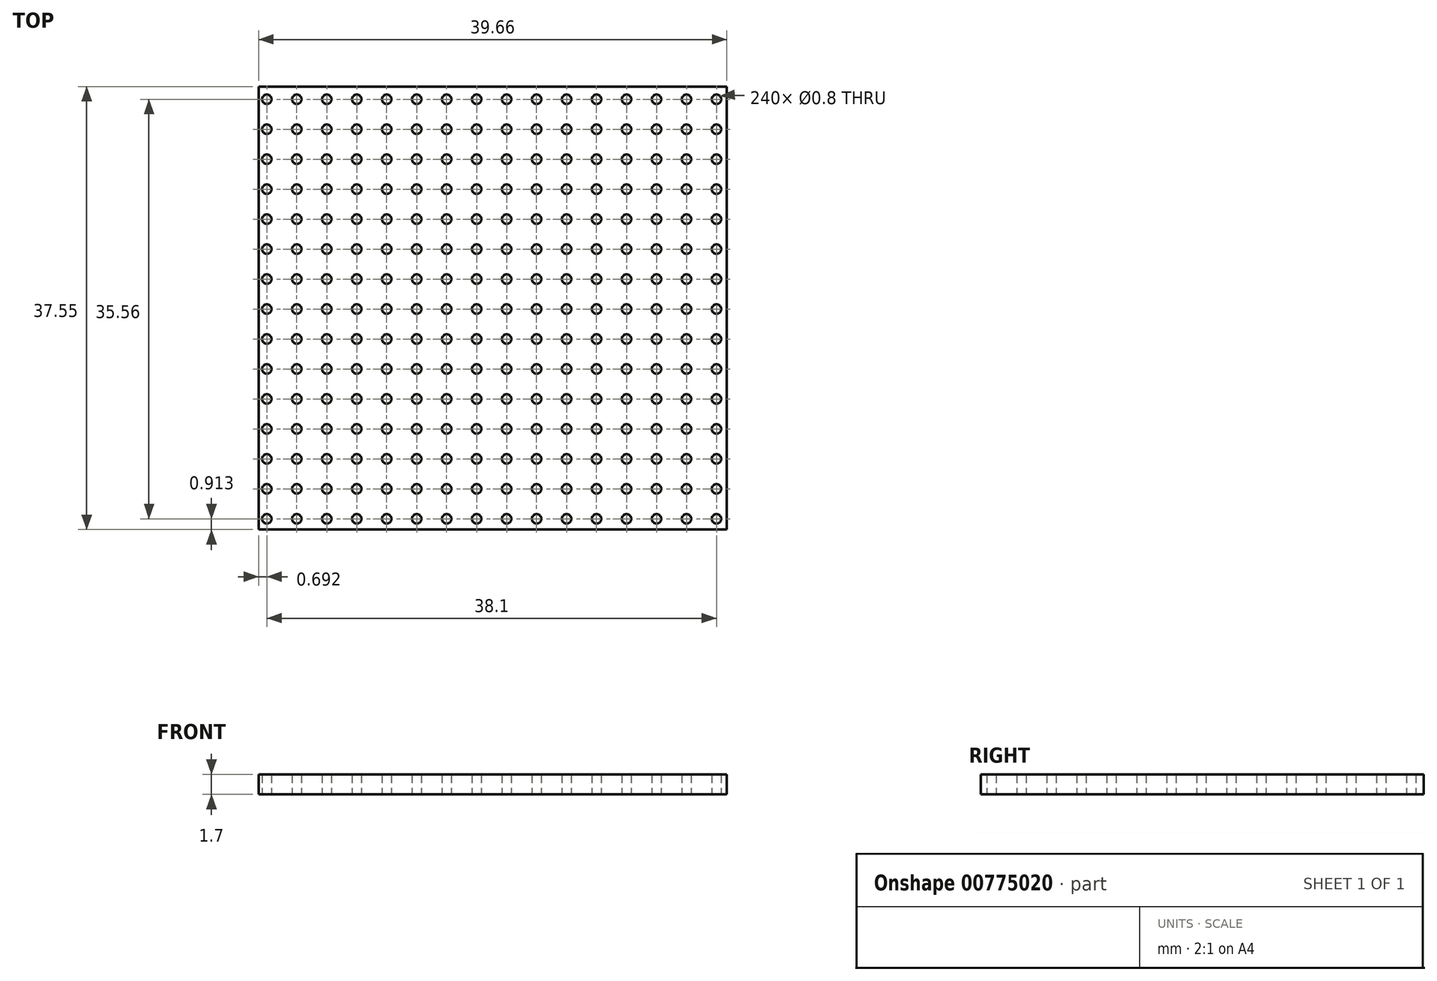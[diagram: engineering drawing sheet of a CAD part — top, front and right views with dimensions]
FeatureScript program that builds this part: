
annotation { "Feature Type Name" : "Feature", "Feature Type Description" : "" }
export const myFeature = defineFeature(function(context is Context, id is Id, definition is map)
    precondition{}
    {
        {
            var Q0;
            Q0=qCreatedBy(makeId("Top.planeOp"),FACE);
            var sketch = newSketch(context, id + "F0", { "sketchPlane" : qUnion([Q0])});
            skCircle(sketch, "E0", {"center": v(-31, -33.54) * mm, "radius": 0.4 * mm});
            skCircle(sketch, "E1.1.0.0", {"center": v(-28.47, -33.54) * mm, "radius": 0.4 * mm});
            skCircle(sketch, "E1.2.0.0", {"center": v(-25.93, -33.54) * mm, "radius": 0.4 * mm});
            skCircle(sketch, "E1.3.0.0", {"center": v(-23.39, -33.54) * mm, "radius": 0.4 * mm});
            skCircle(sketch, "E1.4.0.0", {"center": v(-20.85, -33.54) * mm, "radius": 0.4 * mm});
            skCircle(sketch, "E1.5.0.0", {"center": v(-18.3, -33.54) * mm, "radius": 0.4 * mm});
            skCircle(sketch, "E1.6.0.0", {"center": v(-15.77, -33.54) * mm, "radius": 0.4 * mm});
            skCircle(sketch, "E1.7.0.0", {"center": v(-13.23, -33.54) * mm, "radius": 0.4 * mm});
            skCircle(sketch, "E1.8.0.0", {"center": v(-10.69, -33.54) * mm, "radius": 0.4 * mm});
            skCircle(sketch, "E1.9.0.0", {"center": v(-8.15, -33.54) * mm, "radius": 0.4 * mm});
            skCircle(sketch, "E1.10.0.0", {"center": v(-5.6, -33.54) * mm, "radius": 0.4 * mm});
            skCircle(sketch, "E1.11.0.0", {"center": v(-3.07, -33.54) * mm, "radius": 0.4 * mm});
            skCircle(sketch, "E1.12.0.0", {"center": v(-0.53, -33.54) * mm, "radius": 0.4 * mm});
            skCircle(sketch, "E1.13.0.0", {"center": v(2.01, -33.54) * mm, "radius": 0.4 * mm});
            skCircle(sketch, "E1.14.0.0", {"center": v(4.55, -33.54) * mm, "radius": 0.4 * mm});
            skCircle(sketch, "E1.15.0.0", {"center": v(7.1, -33.54) * mm, "radius": 0.4 * mm});
            skLineSegment(sketch, "E1.direction1", {"start": v(-31, -33.54) * mm, "end": v(-28.47, -33.54) * mm, "construction": true});
            skCircle(sketch, "E2.1.0.0", {"center": v(2.01, -31) * mm, "radius": 0.4 * mm});
            skCircle(sketch, "E2.1.0.1", {"center": v(-0.53, -31) * mm, "radius": 0.4 * mm});
            skCircle(sketch, "E2.1.0.2", {"center": v(-3.07, -31) * mm, "radius": 0.4 * mm});
            skCircle(sketch, "E2.1.0.3", {"center": v(-5.6, -31) * mm, "radius": 0.4 * mm});
            skCircle(sketch, "E2.1.0.4", {"center": v(7.1, -31) * mm, "radius": 0.4 * mm});
            skCircle(sketch, "E2.1.0.5", {"center": v(-8.15, -31) * mm, "radius": 0.4 * mm});
            skCircle(sketch, "E2.1.0.6", {"center": v(-10.69, -31) * mm, "radius": 0.4 * mm});
            skCircle(sketch, "E2.1.0.7", {"center": v(4.55, -31) * mm, "radius": 0.4 * mm});
            skCircle(sketch, "E2.1.0.8", {"center": v(-13.23, -31) * mm, "radius": 0.4 * mm});
            skCircle(sketch, "E2.1.0.9", {"center": v(-15.77, -31) * mm, "radius": 0.4 * mm});
            skCircle(sketch, "E2.1.0.10", {"center": v(-18.3, -31) * mm, "radius": 0.4 * mm});
            skCircle(sketch, "E2.1.0.11", {"center": v(-20.85, -31) * mm, "radius": 0.4 * mm});
            skCircle(sketch, "E2.1.0.12", {"center": v(-23.39, -31) * mm, "radius": 0.4 * mm});
            skCircle(sketch, "E2.1.0.13", {"center": v(-25.93, -31) * mm, "radius": 0.4 * mm});
            skCircle(sketch, "E2.1.0.14", {"center": v(-28.47, -31) * mm, "radius": 0.4 * mm});
            skCircle(sketch, "E2.1.0.15", {"center": v(-31, -31) * mm, "radius": 0.4 * mm});
            skLineSegment(sketch, "E2.1.0.16", {"start": v(-31, -31) * mm, "end": v(-28.47, -31) * mm, "construction": true});
            skCircle(sketch, "E2.2.0.0", {"center": v(2.01, -28.46) * mm, "radius": 0.4 * mm});
            skCircle(sketch, "E2.2.0.1", {"center": v(-0.53, -28.46) * mm, "radius": 0.4 * mm});
            skCircle(sketch, "E2.2.0.2", {"center": v(-3.07, -28.46) * mm, "radius": 0.4 * mm});
            skCircle(sketch, "E2.2.0.3", {"center": v(-5.6, -28.46) * mm, "radius": 0.4 * mm});
            skCircle(sketch, "E2.2.0.4", {"center": v(7.1, -28.46) * mm, "radius": 0.4 * mm});
            skCircle(sketch, "E2.2.0.5", {"center": v(-8.15, -28.46) * mm, "radius": 0.4 * mm});
            skCircle(sketch, "E2.2.0.6", {"center": v(-10.69, -28.46) * mm, "radius": 0.4 * mm});
            skCircle(sketch, "E2.2.0.7", {"center": v(4.55, -28.46) * mm, "radius": 0.4 * mm});
            skCircle(sketch, "E2.2.0.8", {"center": v(-13.23, -28.46) * mm, "radius": 0.4 * mm});
            skCircle(sketch, "E2.2.0.9", {"center": v(-15.77, -28.46) * mm, "radius": 0.4 * mm});
            skCircle(sketch, "E2.2.0.10", {"center": v(-18.3, -28.46) * mm, "radius": 0.4 * mm});
            skCircle(sketch, "E2.2.0.11", {"center": v(-20.85, -28.46) * mm, "radius": 0.4 * mm});
            skCircle(sketch, "E2.2.0.12", {"center": v(-23.39, -28.46) * mm, "radius": 0.4 * mm});
            skCircle(sketch, "E2.2.0.13", {"center": v(-25.93, -28.46) * mm, "radius": 0.4 * mm});
            skCircle(sketch, "E2.2.0.14", {"center": v(-28.47, -28.46) * mm, "radius": 0.4 * mm});
            skCircle(sketch, "E2.2.0.15", {"center": v(-31, -28.46) * mm, "radius": 0.4 * mm});
            skLineSegment(sketch, "E2.2.0.16", {"start": v(-31, -28.46) * mm, "end": v(-28.47, -28.46) * mm, "construction": true});
            skCircle(sketch, "E2.3.0.0", {"center": v(2.01, -25.92) * mm, "radius": 0.4 * mm});
            skCircle(sketch, "E2.3.0.1", {"center": v(-0.53, -25.92) * mm, "radius": 0.4 * mm});
            skCircle(sketch, "E2.3.0.2", {"center": v(-3.07, -25.92) * mm, "radius": 0.4 * mm});
            skCircle(sketch, "E2.3.0.3", {"center": v(-5.6, -25.92) * mm, "radius": 0.4 * mm});
            skCircle(sketch, "E2.3.0.4", {"center": v(7.1, -25.92) * mm, "radius": 0.4 * mm});
            skCircle(sketch, "E2.3.0.5", {"center": v(-8.15, -25.92) * mm, "radius": 0.4 * mm});
            skCircle(sketch, "E2.3.0.6", {"center": v(-10.69, -25.92) * mm, "radius": 0.4 * mm});
            skCircle(sketch, "E2.3.0.7", {"center": v(4.55, -25.92) * mm, "radius": 0.4 * mm});
            skCircle(sketch, "E2.3.0.8", {"center": v(-13.23, -25.92) * mm, "radius": 0.4 * mm});
            skCircle(sketch, "E2.3.0.9", {"center": v(-15.77, -25.92) * mm, "radius": 0.4 * mm});
            skCircle(sketch, "E2.3.0.10", {"center": v(-18.3, -25.92) * mm, "radius": 0.4 * mm});
            skCircle(sketch, "E2.3.0.11", {"center": v(-20.85, -25.92) * mm, "radius": 0.4 * mm});
            skCircle(sketch, "E2.3.0.12", {"center": v(-23.39, -25.92) * mm, "radius": 0.4 * mm});
            skCircle(sketch, "E2.3.0.13", {"center": v(-25.93, -25.92) * mm, "radius": 0.4 * mm});
            skCircle(sketch, "E2.3.0.14", {"center": v(-28.47, -25.92) * mm, "radius": 0.4 * mm});
            skCircle(sketch, "E2.3.0.15", {"center": v(-31, -25.92) * mm, "radius": 0.4 * mm});
            skLineSegment(sketch, "E2.3.0.16", {"start": v(-31, -25.92) * mm, "end": v(-28.47, -25.92) * mm, "construction": true});
            skCircle(sketch, "E2.4.0.0", {"center": v(2.01, -23.38) * mm, "radius": 0.4 * mm});
            skCircle(sketch, "E2.4.0.1", {"center": v(-0.53, -23.38) * mm, "radius": 0.4 * mm});
            skCircle(sketch, "E2.4.0.2", {"center": v(-3.07, -23.38) * mm, "radius": 0.4 * mm});
            skCircle(sketch, "E2.4.0.3", {"center": v(-5.6, -23.38) * mm, "radius": 0.4 * mm});
            skCircle(sketch, "E2.4.0.4", {"center": v(7.1, -23.38) * mm, "radius": 0.4 * mm});
            skCircle(sketch, "E2.4.0.5", {"center": v(-8.15, -23.38) * mm, "radius": 0.4 * mm});
            skCircle(sketch, "E2.4.0.6", {"center": v(-10.69, -23.38) * mm, "radius": 0.4 * mm});
            skCircle(sketch, "E2.4.0.7", {"center": v(4.55, -23.38) * mm, "radius": 0.4 * mm});
            skCircle(sketch, "E2.4.0.8", {"center": v(-13.23, -23.38) * mm, "radius": 0.4 * mm});
            skCircle(sketch, "E2.4.0.9", {"center": v(-15.77, -23.38) * mm, "radius": 0.4 * mm});
            skCircle(sketch, "E2.4.0.10", {"center": v(-18.3, -23.38) * mm, "radius": 0.4 * mm});
            skCircle(sketch, "E2.4.0.11", {"center": v(-20.85, -23.38) * mm, "radius": 0.4 * mm});
            skCircle(sketch, "E2.4.0.12", {"center": v(-23.39, -23.38) * mm, "radius": 0.4 * mm});
            skCircle(sketch, "E2.4.0.13", {"center": v(-25.93, -23.38) * mm, "radius": 0.4 * mm});
            skCircle(sketch, "E2.4.0.14", {"center": v(-28.47, -23.38) * mm, "radius": 0.4 * mm});
            skCircle(sketch, "E2.4.0.15", {"center": v(-31, -23.38) * mm, "radius": 0.4 * mm});
            skLineSegment(sketch, "E2.4.0.16", {"start": v(-31, -23.38) * mm, "end": v(-28.47, -23.38) * mm, "construction": true});
            skCircle(sketch, "E2.5.0.0", {"center": v(2.01, -20.84) * mm, "radius": 0.4 * mm});
            skCircle(sketch, "E2.5.0.1", {"center": v(-0.53, -20.84) * mm, "radius": 0.4 * mm});
            skCircle(sketch, "E2.5.0.2", {"center": v(-3.07, -20.84) * mm, "radius": 0.4 * mm});
            skCircle(sketch, "E2.5.0.3", {"center": v(-5.6, -20.84) * mm, "radius": 0.4 * mm});
            skCircle(sketch, "E2.5.0.4", {"center": v(7.1, -20.84) * mm, "radius": 0.4 * mm});
            skCircle(sketch, "E2.5.0.5", {"center": v(-8.15, -20.84) * mm, "radius": 0.4 * mm});
            skCircle(sketch, "E2.5.0.6", {"center": v(-10.69, -20.84) * mm, "radius": 0.4 * mm});
            skCircle(sketch, "E2.5.0.7", {"center": v(4.55, -20.84) * mm, "radius": 0.4 * mm});
            skCircle(sketch, "E2.5.0.8", {"center": v(-13.23, -20.84) * mm, "radius": 0.4 * mm});
            skCircle(sketch, "E2.5.0.9", {"center": v(-15.77, -20.84) * mm, "radius": 0.4 * mm});
            skCircle(sketch, "E2.5.0.10", {"center": v(-18.3, -20.84) * mm, "radius": 0.4 * mm});
            skCircle(sketch, "E2.5.0.11", {"center": v(-20.85, -20.84) * mm, "radius": 0.4 * mm});
            skCircle(sketch, "E2.5.0.12", {"center": v(-23.39, -20.84) * mm, "radius": 0.4 * mm});
            skCircle(sketch, "E2.5.0.13", {"center": v(-25.93, -20.84) * mm, "radius": 0.4 * mm});
            skCircle(sketch, "E2.5.0.14", {"center": v(-28.47, -20.84) * mm, "radius": 0.4 * mm});
            skCircle(sketch, "E2.5.0.15", {"center": v(-31, -20.84) * mm, "radius": 0.4 * mm});
            skLineSegment(sketch, "E2.5.0.16", {"start": v(-31, -20.84) * mm, "end": v(-28.47, -20.84) * mm, "construction": true});
            skCircle(sketch, "E2.6.0.0", {"center": v(2.01, -18.3) * mm, "radius": 0.4 * mm});
            skCircle(sketch, "E2.6.0.1", {"center": v(-0.53, -18.3) * mm, "radius": 0.4 * mm});
            skCircle(sketch, "E2.6.0.2", {"center": v(-3.07, -18.3) * mm, "radius": 0.4 * mm});
            skCircle(sketch, "E2.6.0.3", {"center": v(-5.6, -18.3) * mm, "radius": 0.4 * mm});
            skCircle(sketch, "E2.6.0.4", {"center": v(7.1, -18.3) * mm, "radius": 0.4 * mm});
            skCircle(sketch, "E2.6.0.5", {"center": v(-8.15, -18.3) * mm, "radius": 0.4 * mm});
            skCircle(sketch, "E2.6.0.6", {"center": v(-10.69, -18.3) * mm, "radius": 0.4 * mm});
            skCircle(sketch, "E2.6.0.7", {"center": v(4.55, -18.3) * mm, "radius": 0.4 * mm});
            skCircle(sketch, "E2.6.0.8", {"center": v(-13.23, -18.3) * mm, "radius": 0.4 * mm});
            skCircle(sketch, "E2.6.0.9", {"center": v(-15.77, -18.3) * mm, "radius": 0.4 * mm});
            skCircle(sketch, "E2.6.0.10", {"center": v(-18.3, -18.3) * mm, "radius": 0.4 * mm});
            skCircle(sketch, "E2.6.0.11", {"center": v(-20.85, -18.3) * mm, "radius": 0.4 * mm});
            skCircle(sketch, "E2.6.0.12", {"center": v(-23.39, -18.3) * mm, "radius": 0.4 * mm});
            skCircle(sketch, "E2.6.0.13", {"center": v(-25.93, -18.3) * mm, "radius": 0.4 * mm});
            skCircle(sketch, "E2.6.0.14", {"center": v(-28.47, -18.3) * mm, "radius": 0.4 * mm});
            skCircle(sketch, "E2.6.0.15", {"center": v(-31, -18.3) * mm, "radius": 0.4 * mm});
            skLineSegment(sketch, "E2.6.0.16", {"start": v(-31, -18.3) * mm, "end": v(-28.47, -18.3) * mm, "construction": true});
            skCircle(sketch, "E2.7.0.0", {"center": v(2.01, -15.76) * mm, "radius": 0.4 * mm});
            skCircle(sketch, "E2.7.0.1", {"center": v(-0.53, -15.76) * mm, "radius": 0.4 * mm});
            skCircle(sketch, "E2.7.0.2", {"center": v(-3.07, -15.76) * mm, "radius": 0.4 * mm});
            skCircle(sketch, "E2.7.0.3", {"center": v(-5.6, -15.76) * mm, "radius": 0.4 * mm});
            skCircle(sketch, "E2.7.0.4", {"center": v(7.1, -15.76) * mm, "radius": 0.4 * mm});
            skCircle(sketch, "E2.7.0.5", {"center": v(-8.15, -15.76) * mm, "radius": 0.4 * mm});
            skCircle(sketch, "E2.7.0.6", {"center": v(-10.69, -15.76) * mm, "radius": 0.4 * mm});
            skCircle(sketch, "E2.7.0.7", {"center": v(4.55, -15.76) * mm, "radius": 0.4 * mm});
            skCircle(sketch, "E2.7.0.8", {"center": v(-13.23, -15.76) * mm, "radius": 0.4 * mm});
            skCircle(sketch, "E2.7.0.9", {"center": v(-15.77, -15.76) * mm, "radius": 0.4 * mm});
            skCircle(sketch, "E2.7.0.10", {"center": v(-18.3, -15.76) * mm, "radius": 0.4 * mm});
            skCircle(sketch, "E2.7.0.11", {"center": v(-20.85, -15.76) * mm, "radius": 0.4 * mm});
            skCircle(sketch, "E2.7.0.12", {"center": v(-23.39, -15.76) * mm, "radius": 0.4 * mm});
            skCircle(sketch, "E2.7.0.13", {"center": v(-25.93, -15.76) * mm, "radius": 0.4 * mm});
            skCircle(sketch, "E2.7.0.14", {"center": v(-28.47, -15.76) * mm, "radius": 0.4 * mm});
            skCircle(sketch, "E2.7.0.15", {"center": v(-31, -15.76) * mm, "radius": 0.4 * mm});
            skLineSegment(sketch, "E2.7.0.16", {"start": v(-31, -15.76) * mm, "end": v(-28.47, -15.76) * mm, "construction": true});
            skCircle(sketch, "E2.8.0.0", {"center": v(2.01, -13.22) * mm, "radius": 0.4 * mm});
            skCircle(sketch, "E2.8.0.1", {"center": v(-0.53, -13.22) * mm, "radius": 0.4 * mm});
            skCircle(sketch, "E2.8.0.2", {"center": v(-3.07, -13.22) * mm, "radius": 0.4 * mm});
            skCircle(sketch, "E2.8.0.3", {"center": v(-5.6, -13.22) * mm, "radius": 0.4 * mm});
            skCircle(sketch, "E2.8.0.4", {"center": v(7.1, -13.22) * mm, "radius": 0.4 * mm});
            skCircle(sketch, "E2.8.0.5", {"center": v(-8.15, -13.22) * mm, "radius": 0.4 * mm});
            skCircle(sketch, "E2.8.0.6", {"center": v(-10.69, -13.22) * mm, "radius": 0.4 * mm});
            skCircle(sketch, "E2.8.0.7", {"center": v(4.55, -13.22) * mm, "radius": 0.4 * mm});
            skCircle(sketch, "E2.8.0.8", {"center": v(-13.23, -13.22) * mm, "radius": 0.4 * mm});
            skCircle(sketch, "E2.8.0.9", {"center": v(-15.77, -13.22) * mm, "radius": 0.4 * mm});
            skCircle(sketch, "E2.8.0.10", {"center": v(-18.3, -13.22) * mm, "radius": 0.4 * mm});
            skCircle(sketch, "E2.8.0.11", {"center": v(-20.85, -13.22) * mm, "radius": 0.4 * mm});
            skCircle(sketch, "E2.8.0.12", {"center": v(-23.39, -13.22) * mm, "radius": 0.4 * mm});
            skCircle(sketch, "E2.8.0.13", {"center": v(-25.93, -13.22) * mm, "radius": 0.4 * mm});
            skCircle(sketch, "E2.8.0.14", {"center": v(-28.47, -13.22) * mm, "radius": 0.4 * mm});
            skCircle(sketch, "E2.8.0.15", {"center": v(-31, -13.22) * mm, "radius": 0.4 * mm});
            skLineSegment(sketch, "E2.8.0.16", {"start": v(-31, -13.22) * mm, "end": v(-28.47, -13.22) * mm, "construction": true});
            skCircle(sketch, "E2.9.0.0", {"center": v(2.01, -10.68) * mm, "radius": 0.4 * mm});
            skCircle(sketch, "E2.9.0.1", {"center": v(-0.53, -10.68) * mm, "radius": 0.4 * mm});
            skCircle(sketch, "E2.9.0.2", {"center": v(-3.07, -10.68) * mm, "radius": 0.4 * mm});
            skCircle(sketch, "E2.9.0.3", {"center": v(-5.6, -10.68) * mm, "radius": 0.4 * mm});
            skCircle(sketch, "E2.9.0.4", {"center": v(7.1, -10.68) * mm, "radius": 0.4 * mm});
            skCircle(sketch, "E2.9.0.5", {"center": v(-8.15, -10.68) * mm, "radius": 0.4 * mm});
            skCircle(sketch, "E2.9.0.6", {"center": v(-10.69, -10.68) * mm, "radius": 0.4 * mm});
            skCircle(sketch, "E2.9.0.7", {"center": v(4.55, -10.68) * mm, "radius": 0.4 * mm});
            skCircle(sketch, "E2.9.0.8", {"center": v(-13.23, -10.68) * mm, "radius": 0.4 * mm});
            skCircle(sketch, "E2.9.0.9", {"center": v(-15.77, -10.68) * mm, "radius": 0.4 * mm});
            skCircle(sketch, "E2.9.0.10", {"center": v(-18.3, -10.68) * mm, "radius": 0.4 * mm});
            skCircle(sketch, "E2.9.0.11", {"center": v(-20.85, -10.68) * mm, "radius": 0.4 * mm});
            skCircle(sketch, "E2.9.0.12", {"center": v(-23.39, -10.68) * mm, "radius": 0.4 * mm});
            skCircle(sketch, "E2.9.0.13", {"center": v(-25.93, -10.68) * mm, "radius": 0.4 * mm});
            skCircle(sketch, "E2.9.0.14", {"center": v(-28.47, -10.68) * mm, "radius": 0.4 * mm});
            skCircle(sketch, "E2.9.0.15", {"center": v(-31, -10.68) * mm, "radius": 0.4 * mm});
            skLineSegment(sketch, "E2.9.0.16", {"start": v(-31, -10.68) * mm, "end": v(-28.47, -10.68) * mm, "construction": true});
            skCircle(sketch, "E2.10.0.0", {"center": v(2.01, -8.14) * mm, "radius": 0.4 * mm});
            skCircle(sketch, "E2.10.0.1", {"center": v(-0.53, -8.14) * mm, "radius": 0.4 * mm});
            skCircle(sketch, "E2.10.0.2", {"center": v(-3.07, -8.14) * mm, "radius": 0.4 * mm});
            skCircle(sketch, "E2.10.0.3", {"center": v(-5.6, -8.14) * mm, "radius": 0.4 * mm});
            skCircle(sketch, "E2.10.0.4", {"center": v(7.1, -8.14) * mm, "radius": 0.4 * mm});
            skCircle(sketch, "E2.10.0.5", {"center": v(-8.15, -8.14) * mm, "radius": 0.4 * mm});
            skCircle(sketch, "E2.10.0.6", {"center": v(-10.69, -8.14) * mm, "radius": 0.4 * mm});
            skCircle(sketch, "E2.10.0.7", {"center": v(4.55, -8.14) * mm, "radius": 0.4 * mm});
            skCircle(sketch, "E2.10.0.8", {"center": v(-13.23, -8.14) * mm, "radius": 0.4 * mm});
            skCircle(sketch, "E2.10.0.9", {"center": v(-15.77, -8.14) * mm, "radius": 0.4 * mm});
            skCircle(sketch, "E2.10.0.10", {"center": v(-18.3, -8.14) * mm, "radius": 0.4 * mm});
            skCircle(sketch, "E2.10.0.11", {"center": v(-20.85, -8.14) * mm, "radius": 0.4 * mm});
            skCircle(sketch, "E2.10.0.12", {"center": v(-23.39, -8.14) * mm, "radius": 0.4 * mm});
            skCircle(sketch, "E2.10.0.13", {"center": v(-25.93, -8.14) * mm, "radius": 0.4 * mm});
            skCircle(sketch, "E2.10.0.14", {"center": v(-28.47, -8.14) * mm, "radius": 0.4 * mm});
            skCircle(sketch, "E2.10.0.15", {"center": v(-31, -8.14) * mm, "radius": 0.4 * mm});
            skLineSegment(sketch, "E2.10.0.16", {"start": v(-31, -8.14) * mm, "end": v(-28.47, -8.14) * mm, "construction": true});
            skCircle(sketch, "E2.11.0.0", {"center": v(2.01, -5.6) * mm, "radius": 0.4 * mm});
            skCircle(sketch, "E2.11.0.1", {"center": v(-0.53, -5.6) * mm, "radius": 0.4 * mm});
            skCircle(sketch, "E2.11.0.2", {"center": v(-3.07, -5.6) * mm, "radius": 0.4 * mm});
            skCircle(sketch, "E2.11.0.3", {"center": v(-5.6, -5.6) * mm, "radius": 0.4 * mm});
            skCircle(sketch, "E2.11.0.4", {"center": v(7.1, -5.6) * mm, "radius": 0.4 * mm});
            skCircle(sketch, "E2.11.0.5", {"center": v(-8.15, -5.6) * mm, "radius": 0.4 * mm});
            skCircle(sketch, "E2.11.0.6", {"center": v(-10.69, -5.6) * mm, "radius": 0.4 * mm});
            skCircle(sketch, "E2.11.0.7", {"center": v(4.55, -5.6) * mm, "radius": 0.4 * mm});
            skCircle(sketch, "E2.11.0.8", {"center": v(-13.23, -5.6) * mm, "radius": 0.4 * mm});
            skCircle(sketch, "E2.11.0.9", {"center": v(-15.77, -5.6) * mm, "radius": 0.4 * mm});
            skCircle(sketch, "E2.11.0.10", {"center": v(-18.3, -5.6) * mm, "radius": 0.4 * mm});
            skCircle(sketch, "E2.11.0.11", {"center": v(-20.85, -5.6) * mm, "radius": 0.4 * mm});
            skCircle(sketch, "E2.11.0.12", {"center": v(-23.39, -5.6) * mm, "radius": 0.4 * mm});
            skCircle(sketch, "E2.11.0.13", {"center": v(-25.93, -5.6) * mm, "radius": 0.4 * mm});
            skCircle(sketch, "E2.11.0.14", {"center": v(-28.47, -5.6) * mm, "radius": 0.4 * mm});
            skCircle(sketch, "E2.11.0.15", {"center": v(-31, -5.6) * mm, "radius": 0.4 * mm});
            skLineSegment(sketch, "E2.11.0.16", {"start": v(-31, -5.6) * mm, "end": v(-28.47, -5.6) * mm, "construction": true});
            skCircle(sketch, "E2.12.0.0", {"center": v(2.01, -3.06) * mm, "radius": 0.4 * mm});
            skCircle(sketch, "E2.12.0.1", {"center": v(-0.53, -3.06) * mm, "radius": 0.4 * mm});
            skCircle(sketch, "E2.12.0.2", {"center": v(-3.07, -3.06) * mm, "radius": 0.4 * mm});
            skCircle(sketch, "E2.12.0.3", {"center": v(-5.6, -3.06) * mm, "radius": 0.4 * mm});
            skCircle(sketch, "E2.12.0.4", {"center": v(7.1, -3.06) * mm, "radius": 0.4 * mm});
            skCircle(sketch, "E2.12.0.5", {"center": v(-8.15, -3.06) * mm, "radius": 0.4 * mm});
            skCircle(sketch, "E2.12.0.6", {"center": v(-10.69, -3.06) * mm, "radius": 0.4 * mm});
            skCircle(sketch, "E2.12.0.7", {"center": v(4.55, -3.06) * mm, "radius": 0.4 * mm});
            skCircle(sketch, "E2.12.0.8", {"center": v(-13.23, -3.06) * mm, "radius": 0.4 * mm});
            skCircle(sketch, "E2.12.0.9", {"center": v(-15.77, -3.06) * mm, "radius": 0.4 * mm});
            skCircle(sketch, "E2.12.0.10", {"center": v(-18.3, -3.06) * mm, "radius": 0.4 * mm});
            skCircle(sketch, "E2.12.0.11", {"center": v(-20.85, -3.06) * mm, "radius": 0.4 * mm});
            skCircle(sketch, "E2.12.0.12", {"center": v(-23.39, -3.06) * mm, "radius": 0.4 * mm});
            skCircle(sketch, "E2.12.0.13", {"center": v(-25.93, -3.06) * mm, "radius": 0.4 * mm});
            skCircle(sketch, "E2.12.0.14", {"center": v(-28.47, -3.06) * mm, "radius": 0.4 * mm});
            skCircle(sketch, "E2.12.0.15", {"center": v(-31, -3.06) * mm, "radius": 0.4 * mm});
            skLineSegment(sketch, "E2.12.0.16", {"start": v(-31, -3.06) * mm, "end": v(-28.47, -3.06) * mm, "construction": true});
            skCircle(sketch, "E2.13.0.0", {"center": v(2.01, -0.52) * mm, "radius": 0.4 * mm});
            skCircle(sketch, "E2.13.0.1", {"center": v(-0.53, -0.52) * mm, "radius": 0.4 * mm});
            skCircle(sketch, "E2.13.0.2", {"center": v(-3.07, -0.52) * mm, "radius": 0.4 * mm});
            skCircle(sketch, "E2.13.0.3", {"center": v(-5.6, -0.52) * mm, "radius": 0.4 * mm});
            skCircle(sketch, "E2.13.0.4", {"center": v(7.1, -0.52) * mm, "radius": 0.4 * mm});
            skCircle(sketch, "E2.13.0.5", {"center": v(-8.15, -0.52) * mm, "radius": 0.4 * mm});
            skCircle(sketch, "E2.13.0.6", {"center": v(-10.69, -0.52) * mm, "radius": 0.4 * mm});
            skCircle(sketch, "E2.13.0.7", {"center": v(4.55, -0.52) * mm, "radius": 0.4 * mm});
            skCircle(sketch, "E2.13.0.8", {"center": v(-13.23, -0.52) * mm, "radius": 0.4 * mm});
            skCircle(sketch, "E2.13.0.9", {"center": v(-15.77, -0.52) * mm, "radius": 0.4 * mm});
            skCircle(sketch, "E2.13.0.10", {"center": v(-18.3, -0.52) * mm, "radius": 0.4 * mm});
            skCircle(sketch, "E2.13.0.11", {"center": v(-20.85, -0.52) * mm, "radius": 0.4 * mm});
            skCircle(sketch, "E2.13.0.12", {"center": v(-23.39, -0.52) * mm, "radius": 0.4 * mm});
            skCircle(sketch, "E2.13.0.13", {"center": v(-25.93, -0.52) * mm, "radius": 0.4 * mm});
            skCircle(sketch, "E2.13.0.14", {"center": v(-28.47, -0.52) * mm, "radius": 0.4 * mm});
            skCircle(sketch, "E2.13.0.15", {"center": v(-31, -0.52) * mm, "radius": 0.4 * mm});
            skLineSegment(sketch, "E2.13.0.16", {"start": v(-31, -0.52) * mm, "end": v(-28.47, -0.52) * mm, "construction": true});
            skCircle(sketch, "E2.14.0.0", {"center": v(2.01, 2.02) * mm, "radius": 0.4 * mm});
            skCircle(sketch, "E2.14.0.1", {"center": v(-0.53, 2.02) * mm, "radius": 0.4 * mm});
            skCircle(sketch, "E2.14.0.2", {"center": v(-3.07, 2.02) * mm, "radius": 0.4 * mm});
            skCircle(sketch, "E2.14.0.3", {"center": v(-5.6, 2.02) * mm, "radius": 0.4 * mm});
            skCircle(sketch, "E2.14.0.4", {"center": v(7.1, 2.02) * mm, "radius": 0.4 * mm});
            skCircle(sketch, "E2.14.0.5", {"center": v(-8.15, 2.02) * mm, "radius": 0.4 * mm});
            skCircle(sketch, "E2.14.0.6", {"center": v(-10.69, 2.02) * mm, "radius": 0.4 * mm});
            skCircle(sketch, "E2.14.0.7", {"center": v(4.55, 2.02) * mm, "radius": 0.4 * mm});
            skCircle(sketch, "E2.14.0.8", {"center": v(-13.23, 2.02) * mm, "radius": 0.4 * mm});
            skCircle(sketch, "E2.14.0.9", {"center": v(-15.77, 2.02) * mm, "radius": 0.4 * mm});
            skCircle(sketch, "E2.14.0.10", {"center": v(-18.3, 2.02) * mm, "radius": 0.4 * mm});
            skCircle(sketch, "E2.14.0.11", {"center": v(-20.85, 2.02) * mm, "radius": 0.4 * mm});
            skCircle(sketch, "E2.14.0.12", {"center": v(-23.39, 2.02) * mm, "radius": 0.4 * mm});
            skCircle(sketch, "E2.14.0.13", {"center": v(-25.93, 2.02) * mm, "radius": 0.4 * mm});
            skCircle(sketch, "E2.14.0.14", {"center": v(-28.47, 2.02) * mm, "radius": 0.4 * mm});
            skCircle(sketch, "E2.14.0.15", {"center": v(-31, 2.02) * mm, "radius": 0.4 * mm});
            skLineSegment(sketch, "E2.14.0.16", {"start": v(-31, 2.02) * mm, "end": v(-28.47, 2.02) * mm, "construction": true});
            skLineSegment(sketch, "E2.direction1", {"start": v(-31, -33.54) * mm, "end": v(-31, -31) * mm, "construction": true});
            skLineSegment(sketch, "E3.bottom", {"start": v(-31.7, 3.1) * mm, "end": v(7.96, 3.1) * mm});
            skLineSegment(sketch, "E3.top", {"start": v(-31.7, -34.45) * mm, "end": v(7.96, -34.45) * mm});
            skLineSegment(sketch, "E3.left", {"start": v(-31.7, 3.1) * mm, "end": v(-31.7, -34.45) * mm});
            skLineSegment(sketch, "E3.right", {"start": v(7.96, 3.1) * mm, "end": v(7.96, -34.45) * mm});
            skSolve(sketch);
        }
        {
            var Q0;
            Q0 = qSketchRegion(id + "F0", true);
            extrude(context, id + "F1", {"entities" : qUnion([Q0]), "depth" : 1.7 * mm, "offsetDistance" : 25 * mm});
        }
    });
